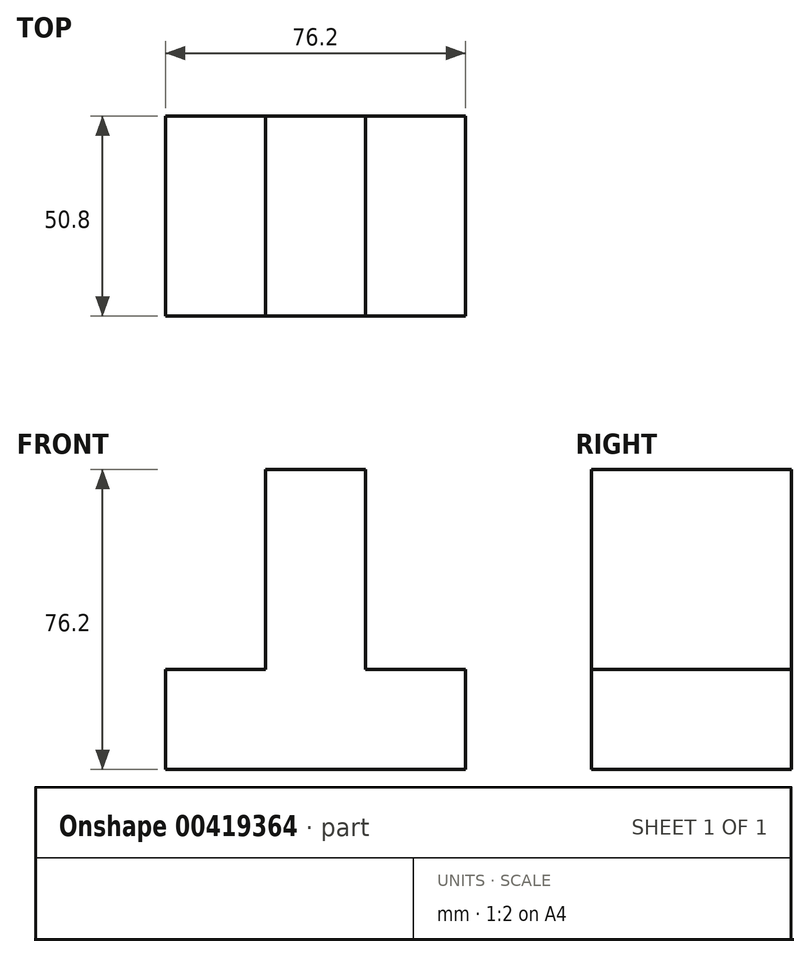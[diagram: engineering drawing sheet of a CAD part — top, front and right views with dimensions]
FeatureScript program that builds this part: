
annotation { "Feature Type Name" : "Feature", "Feature Type Description" : "" }
export const myFeature = defineFeature(function(context is Context, id is Id, definition is map)
    precondition{}
    {
        {
            var Q0;
            Q0=qCreatedBy(makeId("Front.planeOp"),FACE);
            var sketch = newSketch(context, id + "F0", { "sketchPlane" : qUnion([Q0])});
            skLineSegment(sketch, "E0", {"start": v(-29.6, -16.23) * mm, "end": v(46.6, -16.23) * mm});
            skLineSegment(sketch, "E1", {"start": v(46.6, -16.23) * mm, "end": v(46.6, 9.17) * mm});
            skLineSegment(sketch, "E2", {"start": v(46.6, 9.17) * mm, "end": v(21.2, 9.17) * mm});
            skLineSegment(sketch, "E3", {"start": v(21.2, 9.17) * mm, "end": v(21.2, 59.97) * mm});
            skLineSegment(sketch, "E4", {"start": v(21.2, 59.97) * mm, "end": v(-4.2, 59.97) * mm});
            skLineSegment(sketch, "E5", {"start": v(-4.2, 59.97) * mm, "end": v(-4.2, 9.17) * mm});
            skLineSegment(sketch, "E6", {"start": v(-4.2, 9.17) * mm, "end": v(-29.6, 9.17) * mm});
            skLineSegment(sketch, "E7", {"start": v(-29.6, 9.17) * mm, "end": v(-29.6, -16.23) * mm});
            skSolve(sketch);
        }
        {
            var Q0;
            Q0 = qSketchRegion(id + "F0", true);
            extrude(context, id + "F1", {"entities" : qUnion([Q0]), "depth" : 50.8 * mm});
        }
    });
